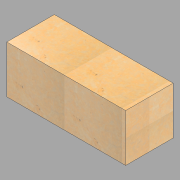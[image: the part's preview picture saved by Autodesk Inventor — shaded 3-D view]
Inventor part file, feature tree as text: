
AUTODESK INVENTOR PART (.ipt)
format: ipt  version: 2022.1 (Build 261234020, 234B)  size: 122,880 bytes
history: native  units: in
note: dims shown in document units (in); Inventor stores cm internally (conversion verified against a paired STEP export)
features: extrude x1, sketch x1
ambient origin geometry x8: Origin, YZ Plane, XZ Plane, XY Plane, X Axis, Y Axis, Z Axis, Center Point
bodies: Solid1 (feature_tree)
feature tree (2):
  extrude  "Extrusion1"  Depth=24.0in
  sketch  "Sketch1"  dims[d0=24.0in d1=24.0in d2=60.0in d3=0.0in]
